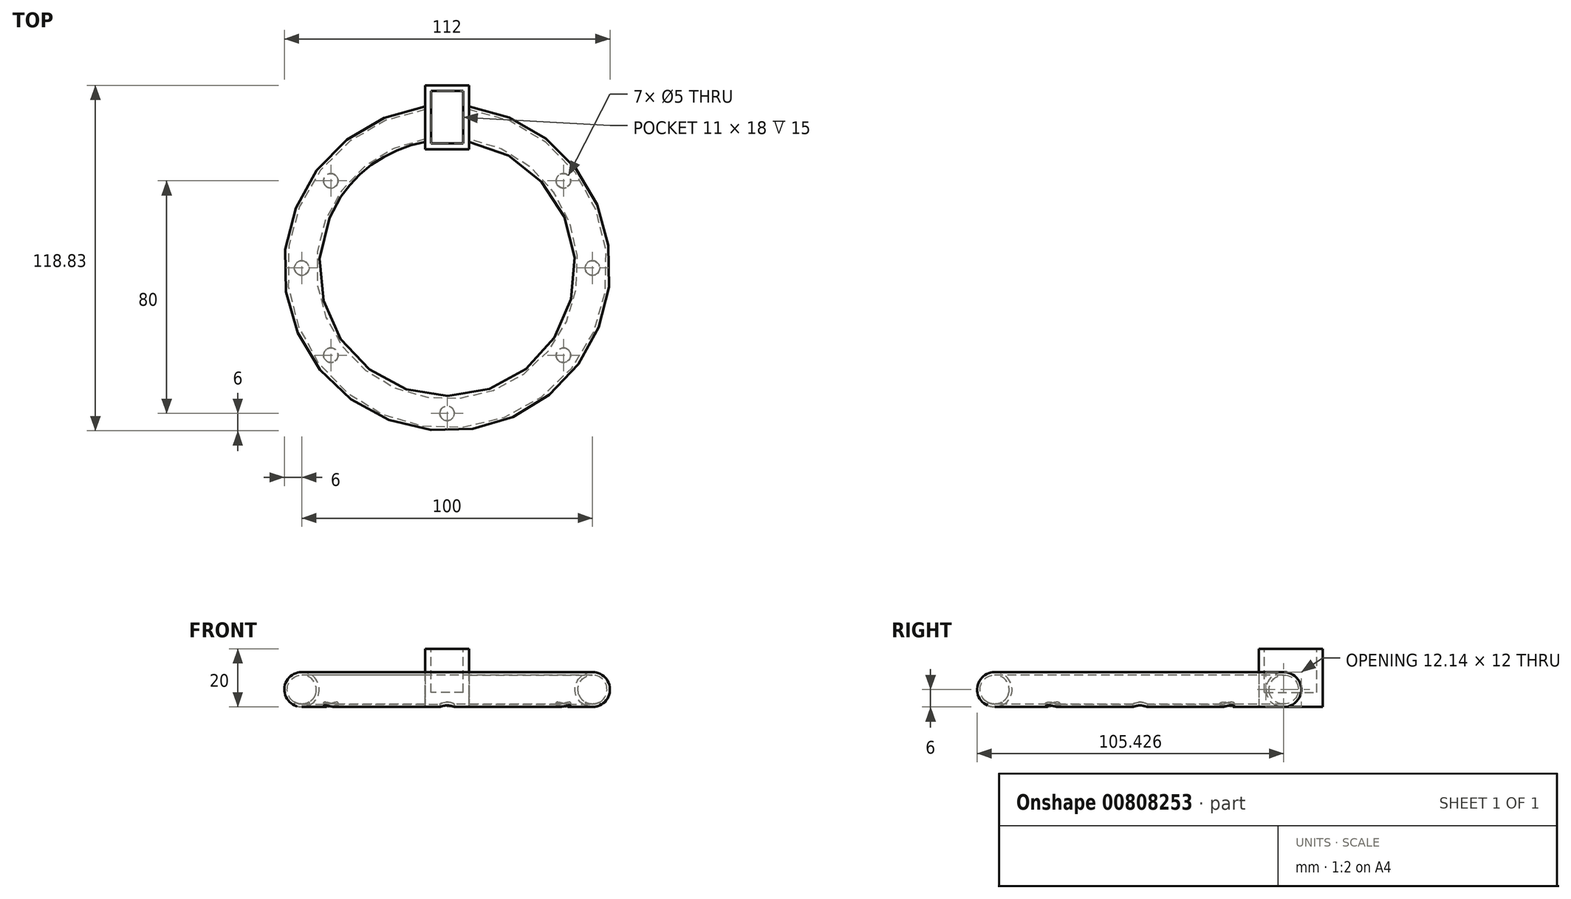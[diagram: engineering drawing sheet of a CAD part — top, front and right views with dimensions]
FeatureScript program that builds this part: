
annotation { "Feature Type Name" : "Feature", "Feature Type Description" : "" }
export const myFeature = defineFeature(function(context is Context, id is Id, definition is map)
    precondition{}
    {
        {
            var Q0;
            Q0=qCreatedBy(makeId("Right.planeOp"),FACE);
            var sketch = newSketch(context, id + "F0", { "sketchPlane" : qUnion([Q0])});
            skCircle(sketch, "E0", {"center": v(-50, 0) * mm, "radius": 5 * mm});
            skCircle(sketch, "E1", {"center": v(-50, 0) * mm, "radius": 6 * mm});
            skSolve(sketch);
        }
        {
            var Q0;
            Q0=qCreatedBy(makeId("Top.planeOp"),FACE);
            var sketch = newSketch(context, id + "F1", { "sketchPlane" : qUnion([Q0])});
            skCircle(sketch, "E2", {"center": v(0, 0) * mm, "radius": 50 * mm});
            skSolve(sketch);
        }
        {
            var Q0;
            Q0=makeQuery(id+"F0.imprint","IMPRINT",FACE,{"disambiguationData":[TD([[makeQuery(id+"F0.imprint","IMPRINT",EDGE,{"derivedFrom":sQuery(id+"F0.wireOp",EDGE,"E0")}),-1.0]])]});
            var Q1;
            Q1=sQuery(id+"F1.wireOp",EDGE,"E2");
            sweep(context, id + "F2", {"profiles" : qUnion([Q0]), "path" : qUnion([Q1])});
        }
        {
            var Q0;
            Q0=qCreatedBy(makeId("Top.planeOp"),FACE);
            cPlane(context, id + "F3", {"entities" : qUnion([Q0]), "cplaneType" : CPlaneType.OFFSET, "offset" : 6 * mm, "oppositeDirection" : true, "width" : 150 * mm, "height" : 150 * mm});
        }
        {
            var Q0;
            Q0=qCreatedBy(id+"F3.planeOp",FACE);
            var sketch = newSketch(context, id + "F4", { "sketchPlane" : qUnion([Q0])});
            skPoint(sketch, "E3.middle", {"position": v(0, 0) * mm});
            skCircle(sketch, "E4", {"center": v(-40, -30) * mm, "radius": 2.5 * mm});
            skCircle(sketch, "E5", {"center": v(0, -50) * mm, "radius": 2.5 * mm});
            skCircle(sketch, "E6", {"center": v(40, -30) * mm, "radius": 2.5 * mm});
            skCircle(sketch, "E7", {"center": v(50, 0) * mm, "radius": 2.5 * mm});
            skCircle(sketch, "E8", {"center": v(40, 30) * mm, "radius": 2.5 * mm});
            skCircle(sketch, "E9", {"center": v(-40, 30) * mm, "radius": 2.5 * mm});
            skCircle(sketch, "E10", {"center": v(-50, 0) * mm, "radius": 2.5 * mm});
            skSolve(sketch);
        }
        {
            var Q0;
            Q0 = qSketchRegion(id + "F4", true);
            extrude(context, id + "F5", {"entities" : qUnion([Q0]), "operationType" : NewBodyOperationType.REMOVE, "depth" : 5 * mm, "offsetDistance" : 25 * mm});
        }
        {
            var Q0;
            Q0=qCreatedBy(id+"F3.planeOp",FACE);
            cPlane(context, id + "F6", {"entities" : qUnion([Q0]), "cplaneType" : CPlaneType.OFFSET, "offset" : 10 * mm, "width" : 150 * mm, "height" : 150 * mm});
        }
        {
            var Q0;
            Q0=qCreatedBy(id+"F6.planeOp",FACE);
            var sketch = newSketch(context, id + "F7", { "sketchPlane" : qUnion([Q0])});
            skLineSegment(sketch, "E11.bottom", {"start": v(7.5, 40.83) * mm, "end": v(-7.5, 40.83) * mm});
            skLineSegment(sketch, "E11.top", {"start": v(7.5, 62.83) * mm, "end": v(-7.5, 62.83) * mm});
            skLineSegment(sketch, "E11.left", {"start": v(7.5, 40.83) * mm, "end": v(7.5, 62.83) * mm});
            skLineSegment(sketch, "E11.right", {"start": v(-7.5, 40.83) * mm, "end": v(-7.5, 62.83) * mm});
            skPoint(sketch, "E11.middle", {"position": v(0, 51.83) * mm});
            skSolve(sketch);
        }
        {
            var Q0;
            Q0=makeQuery(id+"F7.imprint","IMPRINT",FACE,{"disambiguationData":[TD([[makeQuery(id+"F7.imprint","IMPRINT",EDGE,{"derivedFrom":sQuery(id+"F7.wireOp",EDGE,"E11.bottom")}),-1.0]])]});
            extrude(context, id + "F8", {"entities" : qUnion([Q0]), "operationType" : NewBodyOperationType.ADD, "endBound" : BoundingType.SYMMETRIC, "depth" : 20 * mm, "offsetDistance" : 25 * mm});
        }
        {
            var Q0;
            Q0=makeQuery(id+"F8.opExtrude","CAP_FACE",FACE,{"disambiguationData":[OSD([sQuery(id+"F7.wireOp",EDGE,"E11.bottom"),sQuery(id+"F7.wireOp",EDGE,"E11.top"),sQuery(id+"F7.wireOp",EDGE,"E11.left"),sQuery(id+"F7.wireOp",EDGE,"E11.right")])],"isStart":false});
            var sketch = newSketch(context, id + "F9", { "sketchPlane" : qUnion([Q0])});
            skLineSegment(sketch, "E12.0", {"start": v(-5.5, 42.83) * mm, "end": v(-5.5, 60.83) * mm});
            skLineSegment(sketch, "E12.1", {"start": v(5.5, 42.83) * mm, "end": v(-5.5, 42.83) * mm});
            skLineSegment(sketch, "E12.2", {"start": v(5.5, 42.83) * mm, "end": v(5.5, 60.83) * mm});
            skLineSegment(sketch, "E12.3", {"start": v(5.5, 60.83) * mm, "end": v(-5.5, 60.83) * mm});
            skSolve(sketch);
        }
        {
            var Q0;
            Q0=makeQuery(id+"F9.imprint","IMPRINT",FACE,{"disambiguationData":[TD([[makeQuery(id+"F9.imprint","IMPRINT",EDGE,{"derivedFrom":sQuery(id+"F9.wireOp",EDGE,"E12.0")}),-1.0]])]});
            extrude(context, id + "F10", {"entities" : qUnion([Q0]), "operationType" : NewBodyOperationType.REMOVE, "oppositeDirection" : true, "depth" : 15 * mm, "offsetDistance" : 25 * mm});
        }
    });
